# Revit family: MaviGard yangın alarm zili
name_source: partatom
category: Fire Alarm Devices
units: mm (PartAtom-declared; Revit-internal decimal feet)

## family parameters
Cut with Voids When Loaded = No
Host = Face
Maintain Annotation Orientation = Yes
OmniClass Number = 23.85.30.21
OmniClass Title = Environmental Detection/Registration
Part Type = Normal
Room Calculation Point = No
Round Connector Dimension = Use Diameter
Shared = No

## types (1)
- MaviGard konvansiyonel yangın alarm zili
    Code Performance = EN 54-3
    Color = Kırmızı
    Cost = 0 $
    Default Elevation = 0 mm  [stored 0 ft]
    Description = Yangın alarm zili
    Fax Number = (+)90 216 466 45 10
    Installation Manual = https://mavilielektronik.com
    Main Material = Red Metal
    Manufacturer = Mavili Elektronik Ticaret A.Ş.
    Model = MaviGard
    Mounting height = Zeminden 2,4 m yukarıda
    Mounting surface = Duvara montaj
    Nominal Depth = 55 mm
    Nominal Height = 150 mm
    Nominal Width = 150 mm
    Operating temperature = (-10°C) - (+55°C)
    Operating voltage range = 18-33V/DC
    Operatonal Voltage (default) = 24 V/DC
    Product Code = MG-5400
    Protection Sign = IP 51
    Public Works Pose Number = 833-598
    Secondary Material = Metal
    URL = https://www.mavili.com.tr
    Warranty Duration Labor = 2
    Warranty Duration Parts = 2
    Warranty Duration Unit = Year
    Weight = 610 gr

note: [stored X ft] marks values corroborated as IEEE doubles in the binary element streams (Revit-internal decimal feet)

## geometry (parser evidence)
native form markers: Sweep x3
no freeform markers — native parametric forms only
